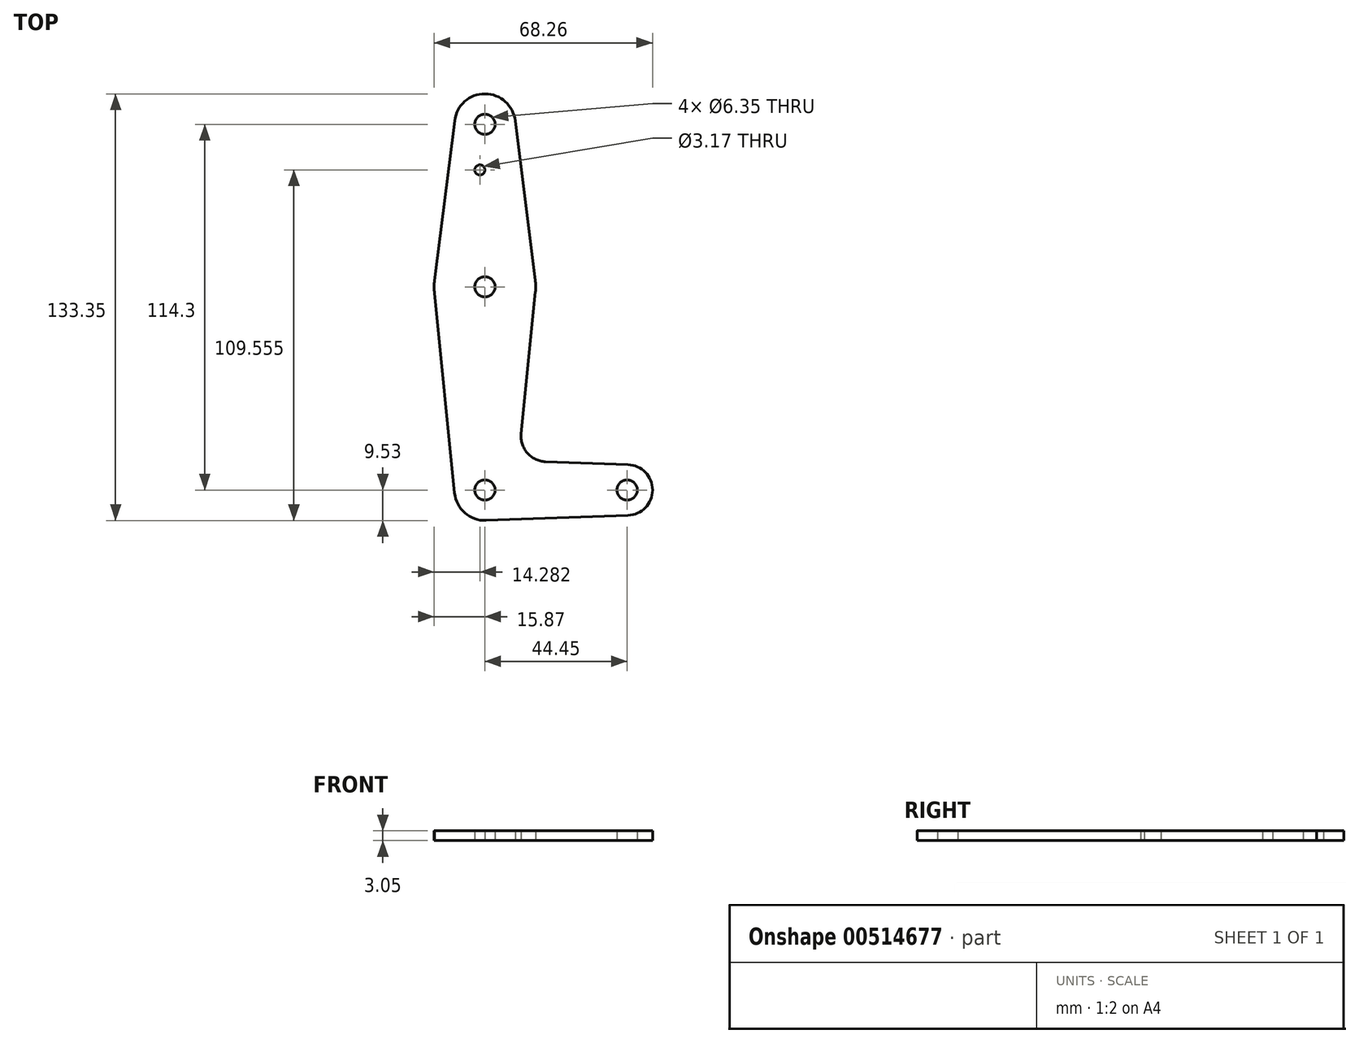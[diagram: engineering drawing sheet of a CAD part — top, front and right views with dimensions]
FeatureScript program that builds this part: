
annotation { "Feature Type Name" : "Feature", "Feature Type Description" : "" }
export const myFeature = defineFeature(function(context is Context, id is Id, definition is map)
    precondition{}
    {
        {
            var Q0;
            Q0=qCreatedBy(makeId("Top.planeOp"),FACE);
            var sketch = newSketch(context, id + "F0", { "sketchPlane" : qUnion([Q0])});
            skLineSegment(sketch, "E0", {"start": v(0, 50.8) * mm, "end": v(0, -63.5) * mm, "construction": true});
            skCircle(sketch, "E1", {"center": v(0, 50.8) * mm, "radius": 9.53 * mm});
            skCircle(sketch, "E2", {"center": v(0, 0) * mm, "radius": 15.88 * mm});
            skCircle(sketch, "E3", {"center": v(0, -63.5) * mm, "radius": 9.53 * mm});
            skLineSegment(sketch, "E4", {"start": v(0, -63.5) * mm, "end": v(44.45, -63.5) * mm, "construction": true});
            skCircle(sketch, "E5", {"center": v(44.45, -63.5) * mm, "radius": 7.94 * mm});
            skLineSegment(sketch, "E6", {"start": v(-9.46, 51.93) * mm, "end": v(-15.75, 1.98) * mm});
            skLineSegment(sketch, "E7", {"start": v(9.47, 51.84) * mm, "end": v(15.75, 1.98) * mm});
            skLineSegment(sketch, "E8", {"start": v(-15.75, -1.98) * mm, "end": v(-9.48, -64.45) * mm});
            skPoint(sketch, "E9.orphan", {"position": v(16, 0) * mm});
            skLineSegment(sketch, "E10", {"start": v(18.97, -54.65) * mm, "end": v(44.73, -55.57) * mm});
            skLineSegment(sketch, "E11", {"start": v(0.34, -73.02) * mm, "end": v(44.73, -71.43) * mm});
            skLineSegment(sketch, "E12", {"start": v(11.34, -45.9) * mm, "end": v(15.8, -1.59) * mm});
            skCircle(sketch, "E13", {"center": v(0, 50.8) * mm, "radius": 3.18 * mm});
            skCircle(sketch, "E14", {"center": v(0, 0) * mm, "radius": 3.18 * mm});
            skCircle(sketch, "E15", {"center": v(0, -63.5) * mm, "radius": 3.18 * mm});
            skCircle(sketch, "E16", {"center": v(44.45, -63.5) * mm, "radius": 3.18 * mm});
            skCircle(sketch, "E17", {"center": v(-1.59, 36.53) * mm, "radius": 1.59 * mm});
            skArc(sketch, "E18.filletArc", {"start": v(11.34, -45.9) * mm, "mid": v(13.26, -51.93) * mm, "end": v(18.97, -54.65) * mm});
            skSolve(sketch);
        }
        {
            var Q0;
            Q0 = qSketchRegion(id + "F0", true);
            extrude(context, id + "F1", {"entities" : qUnion([Q0]), "depth" : 3.05 * mm, "offsetDistance" : 25.4 * mm});
        }
    });
